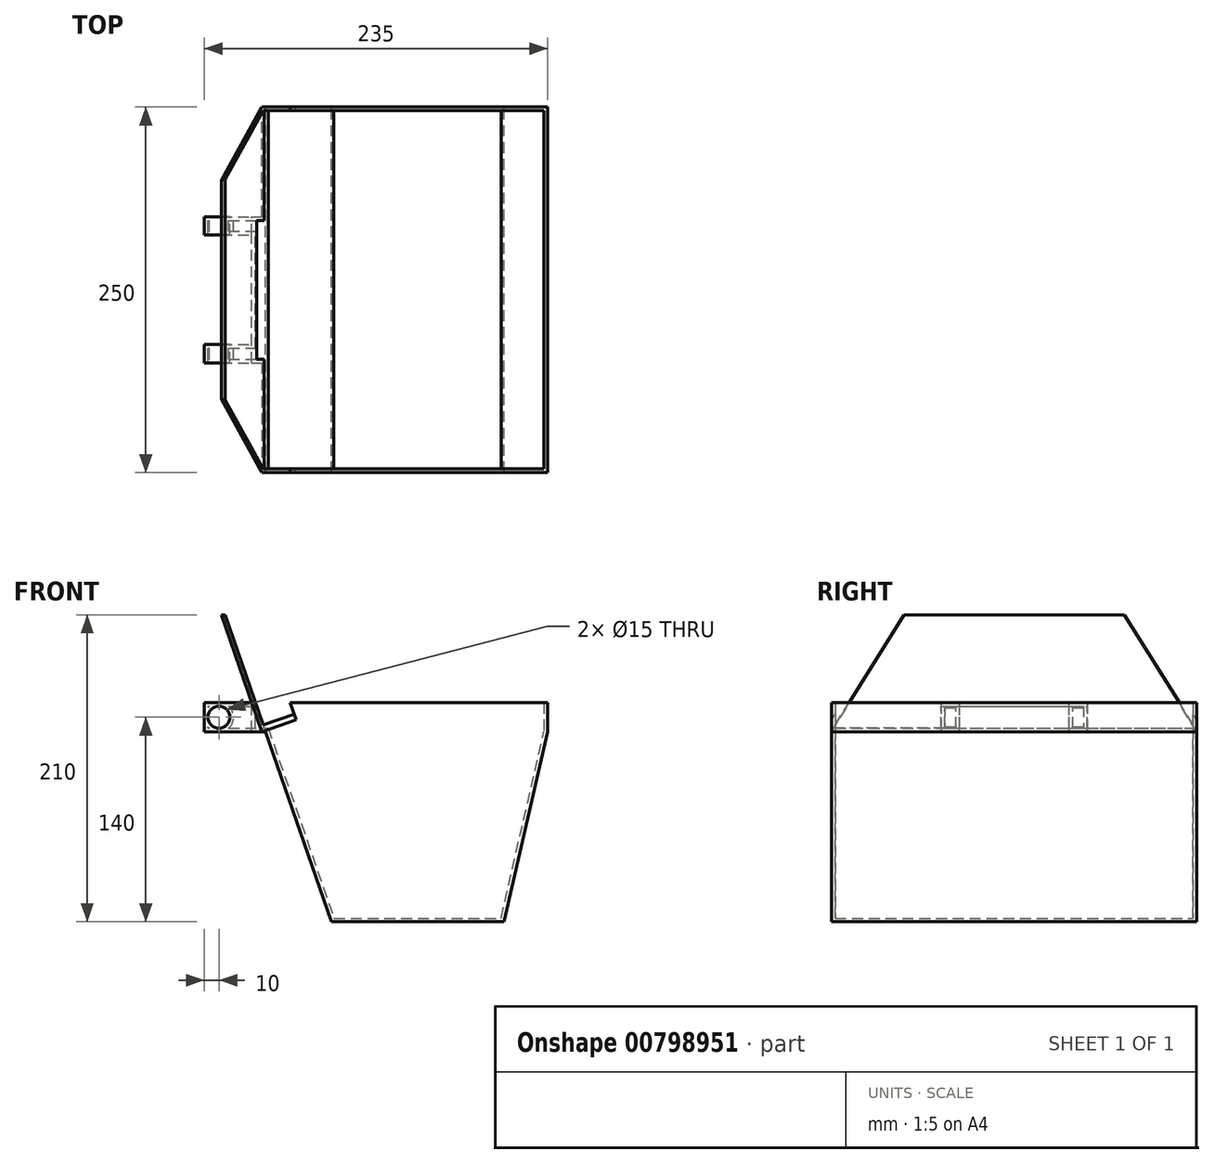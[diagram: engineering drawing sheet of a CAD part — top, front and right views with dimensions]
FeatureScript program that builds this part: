
annotation { "Feature Type Name" : "Feature", "Feature Type Description" : "" }
export const myFeature = defineFeature(function(context is Context, id is Id, definition is map)
    precondition{}
    {
        {
            var Q0;
            Q0=qCreatedBy(makeId("Front.planeOp"),FACE);
            var sketch = newSketch(context, id + "F0", { "sketchPlane" : qUnion([Q0])});
            skLineSegment(sketch, "E0.bottom", {"start": v(0, 0) * mm, "end": v(200, 0) * mm, "construction": true});
            skLineSegment(sketch, "E0.top", {"start": v(0, -150) * mm, "end": v(200, -150) * mm, "construction": true});
            skLineSegment(sketch, "E0.left", {"start": v(0, 0) * mm, "end": v(0, -150) * mm, "construction": true});
            skLineSegment(sketch, "E0.right", {"start": v(200, 0) * mm, "end": v(200, -150) * mm, "construction": true});
            skLineSegment(sketch, "E1.bottom", {"start": v(0, 0) * mm, "end": v(-35, 0) * mm, "construction": true});
            skLineSegment(sketch, "E1.top", {"start": v(0, -20) * mm, "end": v(-35, -20) * mm, "construction": true});
            skLineSegment(sketch, "E1.left", {"start": v(0, 0) * mm, "end": v(0, -20) * mm, "construction": true});
            skLineSegment(sketch, "E1.right", {"start": v(-35, 0) * mm, "end": v(-35, -20) * mm, "construction": true});
            skLineSegment(sketch, "E2", {"start": v(-35, 0) * mm, "end": v(-35, -20) * mm});
            skLineSegment(sketch, "E3", {"start": v(-35, -20) * mm, "end": v(0, -20) * mm});
            skLineSegment(sketch, "E4", {"start": v(0, 0) * mm, "end": v(0, -20) * mm});
            skLineSegment(sketch, "E5", {"start": v(-35, 0) * mm, "end": v(0, 0) * mm});
            skLineSegment(sketch, "E6", {"start": v(0, -20) * mm, "end": v(45, -150) * mm, "construction": true});
            skLineSegment(sketch, "E7", {"start": v(45, -150) * mm, "end": v(170, -150) * mm});
            skLineSegment(sketch, "E8", {"start": v(170, -150) * mm, "end": v(200, 0) * mm, "construction": true});
            skLineSegment(sketch, "E9", {"start": v(0, 0) * mm, "end": v(200, 0) * mm});
            skLineSegment(sketch, "E10", {"start": v(200, 0) * mm, "end": v(200, -20) * mm});
            skLineSegment(sketch, "E11", {"start": v(200, -20) * mm, "end": v(200, -20) * mm});
            skLineSegment(sketch, "E12", {"start": v(170, -150) * mm, "end": v(200, -20) * mm});
            skLineSegment(sketch, "E13", {"start": v(0, 0) * mm, "end": v(-20.77, 60) * mm});
            skLineSegment(sketch, "E14", {"start": v(-20.77, 60) * mm, "end": v(-20.77, 60) * mm});
            skLineSegment(sketch, "E15", {"start": v(-20.77, 60) * mm, "end": v(-27.7, 60) * mm});
            skLineSegment(sketch, "E16", {"start": v(-27.7, 60) * mm, "end": v(0, -20) * mm, "construction": true});
            skLineSegment(sketch, "E17", {"start": v(-35, -10) * mm, "end": v(0, -10) * mm, "construction": true});
            skCircle(sketch, "E18", {"center": v(-25, -10) * mm, "radius": 7.5 * mm});
            skLineSegment(sketch, "E19", {"start": v(13.72, -148.38) * mm, "end": v(0.28, -19.82) * mm, "construction": true});
            skLineSegment(sketch, "E20", {"start": v(0, 0) * mm, "end": v(51.92, -150) * mm});
            skLineSegment(sketch, "E21", {"start": v(0, -20) * mm, "end": v(6.92, -20) * mm});
            skLineSegment(sketch, "E22", {"start": v(-23.41, 60) * mm, "end": v(-2.65, 0) * mm});
            skSolve(sketch);
        }
        {
            var Q0;
            Q0=makeQuery(id+"F0.imprint","IMPRINT",FACE,{"disambiguationData":[TD([[makeQuery(id+"F0.imprint","IMPRINT",EDGE,{"derivedFrom":sQuery(id+"F0.wireOp",EDGE,"E4")}),1.0]])]});
            var Q1;
            {var subQ4=sQuery(id+"F0.wireOp",EDGE,"E2");Q1=makeQuery(id+"F0.imprint","IMPRINT",FACE,{"disambiguationData":[TD([[makeQuery(id+"F0.imprint","IMPRINT",EDGE,{"derivedFrom":subQ4}),1.0]])]});}
            var Q2;
            {var subQ0=sQuery(id+"F0.wireOp",EDGE,"E4");Q2=makeQuery(id+"F0.imprint","IMPRINT",FACE,{"disambiguationData":[TD([[makeQuery(id+"F0.imprint","IMPRINT",EDGE,{"derivedFrom":subQ0}),-1.0]])]});}
            var Q3;
            {var subQ0=sQuery(id+"F0.wireOp",EDGE,"E13");Q3=makeQuery(id+"F0.imprint","IMPRINT",FACE,{"disambiguationData":[TD([[makeQuery(id+"F0.imprint","IMPRINT",EDGE,{"derivedFrom":subQ0}),1.0]])]});}
            var Q4;
            {var subQ1=sQuery(id+"F0.wireOp",EDGE,"E9");Q4=makeQuery(id+"F0.imprint","IMPRINT",FACE,{"disambiguationData":[TD([[makeQuery(id+"F0.imprint","IMPRINT",EDGE,{"derivedFrom":subQ1}),-1.0]])]});}
            extrude(context, id + "F1", {"entities" : qUnion([Q0, Q1, Q2, Q3, Q4]), "endBound" : BoundingType.SYMMETRIC, "depth" : 250 * mm, "offsetDistance" : 25 * mm});
        }
        {
            var Q0;
            Q0=makeQuery(id+"F1.opExtrude","CAP_FACE",FACE,{"disambiguationData":[OSD([sQuery(id+"F0.wireOp",EDGE,"E2"),sQuery(id+"F0.wireOp",EDGE,"E3"),sQuery(id+"F0.wireOp",EDGE,"E5"),sQuery(id+"F0.wireOp",EDGE,"E6"),sQuery(id+"F0.wireOp",EDGE,"E7"),sQuery(id+"F0.wireOp",EDGE,"E9"),sQuery(id+"F0.wireOp",EDGE,"E10"),sQuery(id+"F0.wireOp",EDGE,"E12"),sQuery(id+"F0.wireOp",EDGE,"E13"),sQuery(id+"F0.wireOp",EDGE,"E15"),sQuery(id+"F0.wireOp",EDGE,"E16"),sQuery(id+"F0.wireOp",EDGE,"E18")])],"isStart":false});
            var sketch = newSketch(context, id + "F2", { "sketchPlane" : qUnion([Q0])});
            skLineSegment(sketch, "E23", {"start": v(-55.93, -19.67) * mm, "end": v(-90.82, -19.58) * mm});
            skLineSegment(sketch, "E24", {"start": v(-35, -20) * mm, "end": v(-47.38, -20.3) * mm});
            skLineSegment(sketch, "E25", {"start": v(-54.13, -45.63) * mm, "end": v(-110, -40) * mm});
            skLineSegment(sketch, "E26", {"start": v(-35, 0) * mm, "end": v(-46.2, 5.07) * mm});
            skLineSegment(sketch, "E27", {"start": v(-35, 0) * mm, "end": v(-2.65, 0) * mm});
            skLineSegment(sketch, "E28", {"start": v(-2.65, 0) * mm, "end": v(4.28, -20) * mm});
            skLineSegment(sketch, "E29", {"start": v(4.28, -20) * mm, "end": v(4.28, -20) * mm});
            skLineSegment(sketch, "E30", {"start": v(4.28, -20) * mm, "end": v(-35, -20) * mm});
            skLineSegment(sketch, "E31", {"start": v(-35, 0) * mm, "end": v(-35, -20) * mm});
            skSolve(sketch);
        }
        {
            var Q0;
            Q0=makeQuery(id+"F2.imprint","IMPRINT",FACE,{"disambiguationData":[TD([[makeQuery(id+"F2.imprint","IMPRINT",EDGE,{"derivedFrom":sQuery(id+"F2.wireOp",EDGE,"E27")}),-1.0]])]});
            extrude(context, id + "F3", {"entities" : qUnion([Q0]), "operationType" : NewBodyOperationType.REMOVE, "oppositeDirection" : true, "depth" : 75 * mm, "offsetDistance" : 25 * mm});
        }
        {
            var Q0;
            Q0=makeQuery(id+"F1.opExtrude","CAP_FACE",FACE,{"disambiguationData":[OSD([sQuery(id+"F0.wireOp",EDGE,"E2"),sQuery(id+"F0.wireOp",EDGE,"E3"),sQuery(id+"F0.wireOp",EDGE,"E5"),sQuery(id+"F0.wireOp",EDGE,"E6"),sQuery(id+"F0.wireOp",EDGE,"E7"),sQuery(id+"F0.wireOp",EDGE,"E9"),sQuery(id+"F0.wireOp",EDGE,"E10"),sQuery(id+"F0.wireOp",EDGE,"E12"),sQuery(id+"F0.wireOp",EDGE,"E13"),sQuery(id+"F0.wireOp",EDGE,"E15"),sQuery(id+"F0.wireOp",EDGE,"E16"),sQuery(id+"F0.wireOp",EDGE,"E18")])],"isStart":true});
            var sketch = newSketch(context, id + "F4", { "sketchPlane" : qUnion([Q0])});
            skLineSegment(sketch, "E32", {"start": v(35, -20) * mm, "end": v(46.53, -12.92) * mm});
            skLineSegment(sketch, "E33", {"start": v(76.8, -32.42) * mm, "end": v(190.5, -7.17) * mm});
            skLineSegment(sketch, "E34", {"start": v(35, 0) * mm, "end": v(40.54, -8.33) * mm});
            skLineSegment(sketch, "E35", {"start": v(112.73, -10.66) * mm, "end": v(155, -32.05) * mm});
            skLineSegment(sketch, "E36", {"start": v(35, 0) * mm, "end": v(2.65, 0) * mm});
            skLineSegment(sketch, "E37", {"start": v(2.65, 0) * mm, "end": v(2.65, 0) * mm});
            skLineSegment(sketch, "E38", {"start": v(2.65, 0) * mm, "end": v(-4.28, -20) * mm});
            skLineSegment(sketch, "E39", {"start": v(-4.28, -20) * mm, "end": v(35, -20) * mm});
            skLineSegment(sketch, "E40", {"start": v(35, 0) * mm, "end": v(35, -20) * mm});
            skSolve(sketch);
        }
        {
            var Q0;
            Q0=makeQuery(id+"F4.imprint","IMPRINT",FACE,{"disambiguationData":[TD([[makeQuery(id+"F4.imprint","IMPRINT",EDGE,{"derivedFrom":sQuery(id+"F4.wireOp",EDGE,"E36")}),1.0]])]});
            extrude(context, id + "F5", {"entities" : qUnion([Q0]), "operationType" : NewBodyOperationType.REMOVE, "oppositeDirection" : true, "depth" : 75 * mm, "offsetDistance" : 25 * mm});
        }
        {
            var Q0;
            Q0=makeQuery(id+"F1.opExtrude","SWEPT_FACE",FACE,{"disambiguationData":[OSD([sQuery(id+"F0.wireOp",EDGE,"E5")])]});
            var sketch = newSketch(context, id + "F6", { "sketchPlane" : qUnion([Q0])});
            skLineSegment(sketch, "E41.bottom", {"start": v(-35, -37.5) * mm, "end": v(-2.65, -37.5) * mm});
            skLineSegment(sketch, "E41.top", {"start": v(-35, 37.5) * mm, "end": v(-2.65, 37.5) * mm});
            skLineSegment(sketch, "E41.left", {"start": v(-35, -37.5) * mm, "end": v(-35, 37.5) * mm});
            skLineSegment(sketch, "E41.right", {"start": v(-2.65, -37.5) * mm, "end": v(-2.65, 37.5) * mm});
            skPoint(sketch, "E41.middle", {"position": v(-18.82, 0) * mm});
            skPoint(sketch, "E41.middle.positionSnap0", {"position": v(-18.82, -27.5) * mm});
            skPoint(sketch, "E41.centerSnap0", {"position": v(-18.82, -27.5) * mm});
            skSolve(sketch);
        }
        {
            var Q0;
            Q0=makeQuery(id+"F6.imprint","IMPRINT",FACE,{"disambiguationData":[TD([[makeQuery(id+"F6.imprint","IMPRINT",EDGE,{"derivedFrom":sQuery(id+"F6.wireOp",EDGE,"E41.bottom")}),1.0]])]});
            extrude(context, id + "F7", {"entities" : qUnion([Q0]), "operationType" : NewBodyOperationType.REMOVE, "oppositeDirection" : true, "depth" : 25 * mm, "offsetDistance" : 25 * mm});
        }
        {
            var Q0;
            Q0=makeQuery(id+"F1.opExtrude","SWEPT_FACE",FACE,{"disambiguationData":[OSD([sQuery(id+"F0.wireOp",EDGE,"E9")])]});
            shell(context, id + "F8", {"entities" : qUnion([Q0]), "thickness" : 2.5 * mm});
        }
        {
            var Q0;
            Q0=makeQuery(id+"F5.boolean.opBoolean","MERGE",FACE,{"derivedFrom":[makeQuery(id+"F3.boolean.opBoolean","MERGE",FACE,{"derivedFrom":[makeQuery(id+"F1.opExtrude","SWEPT_FACE",FACE,{"disambiguationData":[OSD([sQuery(id+"F0.wireOp",EDGE,"E22")])]}),makeQuery(id+"F3.opExtrude","SWEPT_FACE",FACE,{"disambiguationData":[OSD([sQuery(id+"F2.wireOp",EDGE,"E28")])]})]}),makeQuery(id+"F5.opExtrude","SWEPT_FACE",FACE,{"disambiguationData":[OSD([sQuery(id+"F4.wireOp",EDGE,"E38")])]})]});
            var sketch = newSketch(context, id + "F9", { "sketchPlane" : qUnion([Q0])});
            skLineSegment(sketch, "E42", {"start": v(-125, -20.3) * mm, "end": v(-75, 64.36) * mm});
            skLineSegment(sketch, "E43", {"start": v(125, -20.3) * mm, "end": v(75, 64.36) * mm});
            skSolve(sketch);
        }
        {
            var Q0;
            {var subQ0=sQuery(id+"F9.wireOp",EDGE,"E42");Q0=makeQuery(id+"F9.imprint","IMPRINT",FACE,{"disambiguationData":[TD([[makeQuery(id+"F9.imprint","IMPRINT",EDGE,{"derivedFrom":subQ0}),1.0]])]});}
            var Q1;
            {var subQ0=sQuery(id+"F9.wireOp",EDGE,"E43");Q1=makeQuery(id+"F9.imprint","IMPRINT",FACE,{"disambiguationData":[TD([[makeQuery(id+"F9.imprint","IMPRINT",EDGE,{"derivedFrom":subQ0}),-1.0]])]});}
            extrude(context, id + "F10", {"entities" : qUnion([Q0, Q1]), "operationType" : NewBodyOperationType.REMOVE, "oppositeDirection" : true, "depth" : 25 * mm, "offsetDistance" : 25 * mm});
        }
    });
